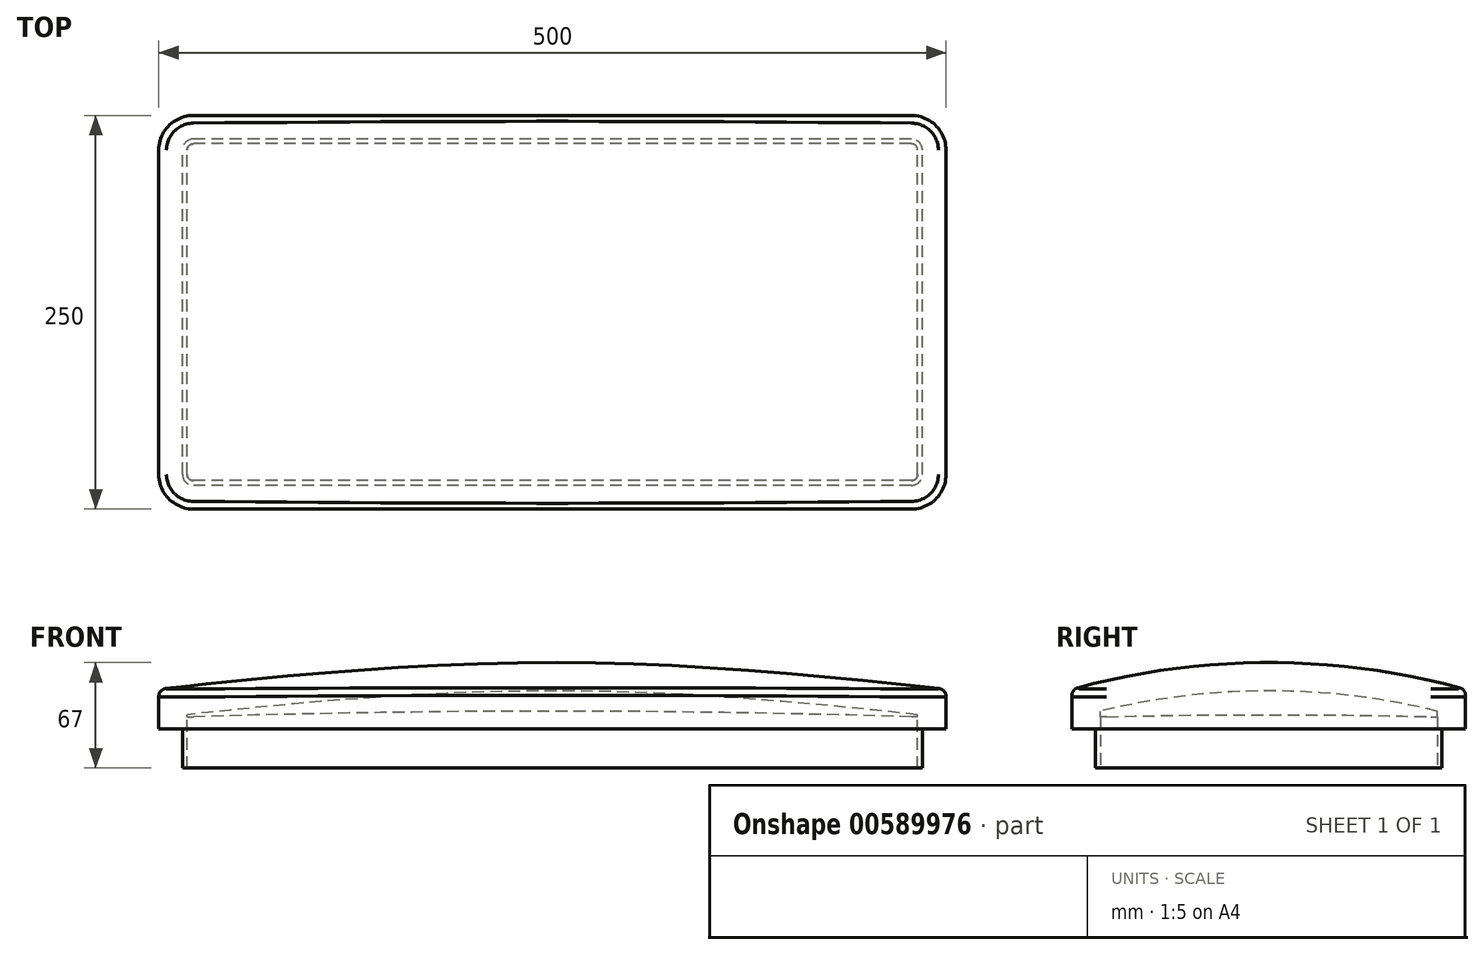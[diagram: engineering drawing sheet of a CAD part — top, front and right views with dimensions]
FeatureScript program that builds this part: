
annotation { "Feature Type Name" : "Feature", "Feature Type Description" : "" }
export const myFeature = defineFeature(function(context is Context, id is Id, definition is map)
    precondition{}
    {
        {
            var Q0;
            Q0=qCreatedBy(makeId("Top.planeOp"),FACE);
            var sketch = newSketch(context, id + "F0", { "sketchPlane" : qUnion([Q0])});
            skLineSegment(sketch, "E0.bottom", {"start": v(250, -125) * mm, "end": v(-250, -125) * mm});
            skLineSegment(sketch, "E0.top", {"start": v(250, 125) * mm, "end": v(-250, 125) * mm});
            skLineSegment(sketch, "E0.left", {"start": v(250, -125) * mm, "end": v(250, 125) * mm});
            skLineSegment(sketch, "E0.right", {"start": v(-250, -125) * mm, "end": v(-250, 125) * mm});
            skPoint(sketch, "E0.middle", {"position": v(0, 0) * mm});
            skSolve(sketch);
        }
        {
            var Q0;
            Q0=qSketchRegion(id+"F0",true);
            extrude(context, id + "F1", {"entities" : qUnion([Q0]), "depth" : 25 * mm});
        }
        {
            var Q0;
            Q0=qCreatedBy(makeId("Right.planeOp"),FACE);
            var sketch = newSketch(context, id + "F2", { "sketchPlane" : qUnion([Q0])});
            skArc(sketch, "E1", {"start": v(125, 25) * mm, "mid": v(0, 42) * mm, "end": v(-125, 25) * mm});
            skLineSegment(sketch, "E2", {"start": v(125, 25) * mm, "end": v(-125, 25) * mm, "construction": true});
            skLineSegment(sketch, "E3.0", {"start": v(-125, 25) * mm, "end": v(-125, 0) * mm});
            skLineSegment(sketch, "E3.1", {"start": v(125, 25) * mm, "end": v(125, 0) * mm});
            skLineSegment(sketch, "E3.2", {"start": v(-125, 0) * mm, "end": v(125, 0) * mm});
            skSolve(sketch);
        }
        {
            var Q0;
            Q0=qCreatedBy(makeId("Front.planeOp"),FACE);
            var sketch = newSketch(context, id + "F3", { "sketchPlane" : qUnion([Q0])});
            skFitSpline(sketch, "E4", {"points": [v(-250, 25) * mm, v(250, 25) * mm], "startDerivative": vector(608.4, 68) * mm, "endDerivative": vector(608.4, -68) * mm});
            skSolve(sketch);
        }
        {
            var Q1;
            Q1=makeQuery(id+"F1.opExtrude","SWEPT_FACE",FACE,{"disambiguationData":[OSD([sQuery(id+"F0.wireOp",EDGE,"E0.left")])]});
            var Q2;
            Q2=makeQuery(id+"F2.imprint","IMPRINT",FACE,{"disambiguationData":[TD([[makeQuery(id+"F2.imprint","IMPRINT",EDGE,{"derivedFrom":sQuery(id+"F2.wireOp",EDGE,"E1")}),1.0]])]});
            var Q3;
            Q3=makeQuery(id+"F1.opExtrude","SWEPT_FACE",FACE,{"disambiguationData":[OSD([sQuery(id+"F0.wireOp",EDGE,"E0.right")])]});
            var Q4;
            Q4=sQuery(id+"F3.wireOp",EDGE,"E4");
            loft(context, id + "F4", {"operationType" : NewBodyOperationType.ADD, "addGuides" : true, "sheetProfilesArray" : [{ "sheetProfileEntities" : qUnion([Q1]) }, { "sheetProfileEntities" : qUnion([Q2]) }, { "sheetProfileEntities" : qUnion([Q3]) }], "guidesArray" : [{ "guideEntities" : qUnion([Q4]), "guideDerivativeType" : LoftGuideDerivativeType.DEFAULT, "guideDerivativeMagnitude" : 1 }]});
        }
        {
            var Q0;
            Q0=makeQuery(id+"F1.opExtrude","SWEPT_EDGE",EDGE,{"disambiguationData":[OSD([sQuery(id+"F0.wireOp",EDGE,"E0.bottom"),sQuery(id+"F0.wireOp",EDGE,"E0.right")])]});
            var Q1;
            Q1=makeQuery(id+"F1.opExtrude","SWEPT_EDGE",EDGE,{"disambiguationData":[OSD([sQuery(id+"F0.wireOp",EDGE,"E0.bottom"),sQuery(id+"F0.wireOp",EDGE,"E0.left")])]});
            var Q2;
            Q2=makeQuery(id+"F1.opExtrude","SWEPT_EDGE",EDGE,{"disambiguationData":[OSD([sQuery(id+"F0.wireOp",EDGE,"E0.top"),sQuery(id+"F0.wireOp",EDGE,"E0.left")])]});
            var Q3;
            Q3=makeQuery(id+"F1.opExtrude","SWEPT_EDGE",EDGE,{"disambiguationData":[OSD([sQuery(id+"F0.wireOp",EDGE,"E0.top"),sQuery(id+"F0.wireOp",EDGE,"E0.right")])]});
            var Q4;
            Q4=makeQuery(id+"Fj6lcFS6ckg576c_1.opPattern","COPY",EDGE,{"derivedFrom":makeQuery(id+"F1.opExtrude","SWEPT_EDGE",EDGE,{"disambiguationData":[OSD([sQuery(id+"F0.wireOp",EDGE,"E0.top"),sQuery(id+"F0.wireOp",EDGE,"E0.right")])]}),"instanceName":"1"});
            var Q5;
            Q5=makeQuery(id+"Fj6lcFS6ckg576c_1.opPattern","COPY",EDGE,{"derivedFrom":makeQuery(id+"F1.opExtrude","SWEPT_EDGE",EDGE,{"disambiguationData":[OSD([sQuery(id+"F0.wireOp",EDGE,"E0.top"),sQuery(id+"F0.wireOp",EDGE,"E0.left")])]}),"instanceName":"1"});
            fillet(context, id + "F5", {"entities" : qUnion([Q0, Q1, Q2, Q3, Q4, Q5]), "radius" : 22 * mm, "tangentPropagation" : true, "allowEdgeOverflow" : false});
        }
        {
            var Q0;
            {var subQ0=sQuery(id+"F0.wireOp",EDGE,"E0.left");Q0=makeQuery(id+"F4.boolean.opBoolean","MERGE",EDGE,{"derivedFrom":[makeQuery(id+"F1.opExtrude","CAP_EDGE",EDGE,{"disambiguationData":[OSD([subQ0])],"isStart":false}),makeQuery(id+"F4.opLoft","MID_CAP_EDGE",EDGE,{"disambiguationData":[OSD([sQuery(id+"F0.wireOp",EDGE,"E0.bottom"),subQ0,sQuery(id+"F3.wireOp",EDGE,"E4")])],"capPos":0.0})]});}
            fillet(context, id + "F6", {"entities" : qUnion([Q0]), "radius" : 5 * mm, "tangentPropagation" : true, "allowEdgeOverflow" : false});
        }
        {
            var Q0;
            Q0=makeQuery(id+"F1.opExtrude","CAP_FACE",FACE,{"disambiguationData":[OSD([sQuery(id+"F0.wireOp",EDGE,"E0.bottom"),sQuery(id+"F0.wireOp",EDGE,"E0.top"),sQuery(id+"F0.wireOp",EDGE,"E0.left"),sQuery(id+"F0.wireOp",EDGE,"E0.right")])],"isStart":true});
            shell(context, id + "F7", {"entities" : qUnion([Q0]), "thickness" : 18 * mm});
        }
        {
            var Q0;
            {var subQ0=makeQuery(id+"FCfvGYRV0cBQWJA_1.splitOp","SPLIT",FACE,{"derivedFrom":makeQuery(id+"F1.opExtrude","CAP_FACE",FACE,{"disambiguationData":[OSD([sQuery(id+"F0.wireOp",EDGE,"E0.bottom"),sQuery(id+"F0.wireOp",EDGE,"E0.top"),sQuery(id+"F0.wireOp",EDGE,"E0.left"),sQuery(id+"F0.wireOp",EDGE,"E0.right")])],"isStart":true}),"isFromBackBody":true});Q0=makeQuery(id+"Fj6lcFS6ckg576c_1.boolean.opBoolean","MERGE",FACE,{"derivedFrom":[subQ0,makeQuery(id+"Fj6lcFS6ckg576c_1.opPattern","COPY",FACE,{"derivedFrom":subQ0,"instanceName":"1"})]});}
            var sketch = newSketch(context, id + "F8", { "sketchPlane" : qUnion([Q0])});
            skArc(sketch, "E5.0", {"start": v(235, 103) * mm, "mid": v(232.95, 107.95) * mm, "end": v(228, 110) * mm});
            skLineSegment(sketch, "E5.1", {"start": v(235, 103) * mm, "end": v(235, -103) * mm});
            skLineSegment(sketch, "E5.2", {"start": v(228, 110) * mm, "end": v(-228, 110) * mm});
            skArc(sketch, "E5.3", {"start": v(228, -110) * mm, "mid": v(232.95, -107.95) * mm, "end": v(235, -103) * mm});
            skArc(sketch, "E5.4", {"start": v(-228, 110) * mm, "mid": v(-232.95, 107.95) * mm, "end": v(-235, 103) * mm});
            skLineSegment(sketch, "E5.5", {"start": v(-235, 103) * mm, "end": v(-235, -103) * mm});
            skArc(sketch, "E5.6", {"start": v(-235, -103) * mm, "mid": v(-232.95, -107.95) * mm, "end": v(-228, -110) * mm});
            skLineSegment(sketch, "E5.7", {"start": v(228, -110) * mm, "end": v(-228, -110) * mm});
            skSolve(sketch);
        }
        {
            var Q0;
            Q0=makeQuery(id+"F8.imprint","IMPRINT",FACE,{"disambiguationData":[TD([[makeQuery(id+"F8.imprint","IMPRINT",EDGE,{"derivedFrom":sQuery(id+"F8.wireOp",EDGE,"E5.0")}),1.0]])]});
            extrude(context, id + "F9", {"entities" : qUnion([Q0]), "operationType" : NewBodyOperationType.ADD, "depth" : 25 * mm});
        }
    });
